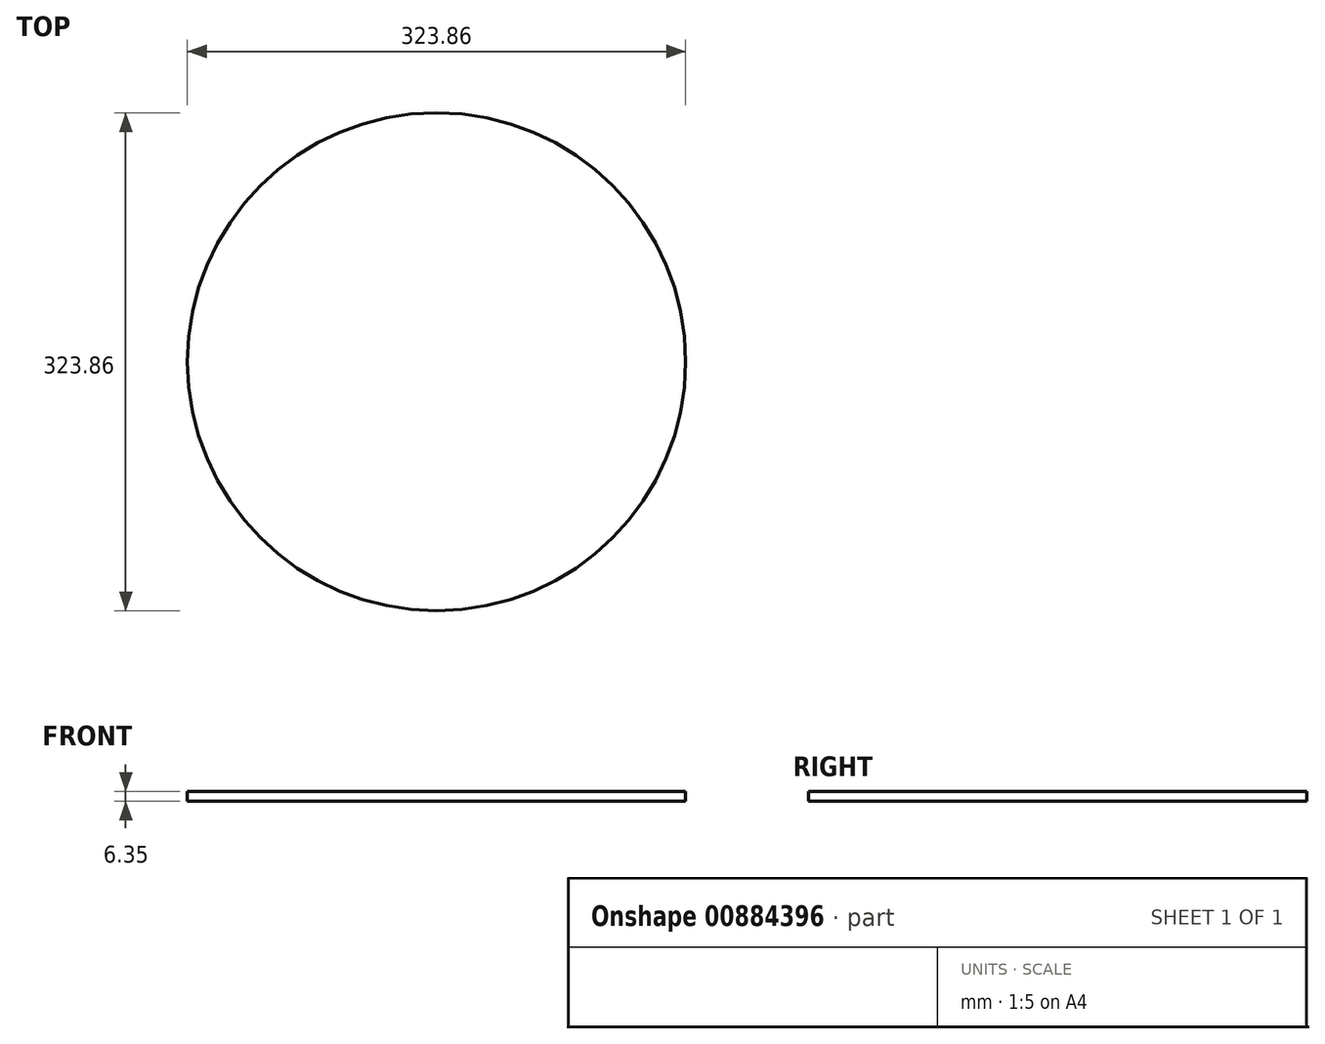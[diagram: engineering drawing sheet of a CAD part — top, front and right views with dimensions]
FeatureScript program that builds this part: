
annotation { "Feature Type Name" : "Feature", "Feature Type Description" : "" }
export const myFeature = defineFeature(function(context is Context, id is Id, definition is map)
    precondition{}
    {
        {
            var Q0;
            Q0=qCreatedBy(makeId("Top.planeOp"),FACE);
            var sketch = newSketch(context, id + "F0", { "sketchPlane" : qUnion([Q0])});
            skCircle(sketch, "E0", {"center": v(0, 0) * mm, "radius": 161.93 * mm});
            skSolve(sketch);
        }
        {
            var Q0;
            Q0 = qSketchRegion(id + "F0", true);
            var Q1;
            Q1=makeQuery(id+"F0.imprint","IMPRINT",FACE,{"disambiguationData":[TD([[makeQuery(id+"F0.imprint","IMPRINT",EDGE,{"derivedFrom":sQuery(id+"F0.wireOp",EDGE,"E0")}),1.0]])]});
            extrude(context, id + "F1", {"entities" : qUnion([Q0, Q1]), "depth" : 6.35 * mm, "offsetDistance" : 25.4 * mm});
        }
    });
